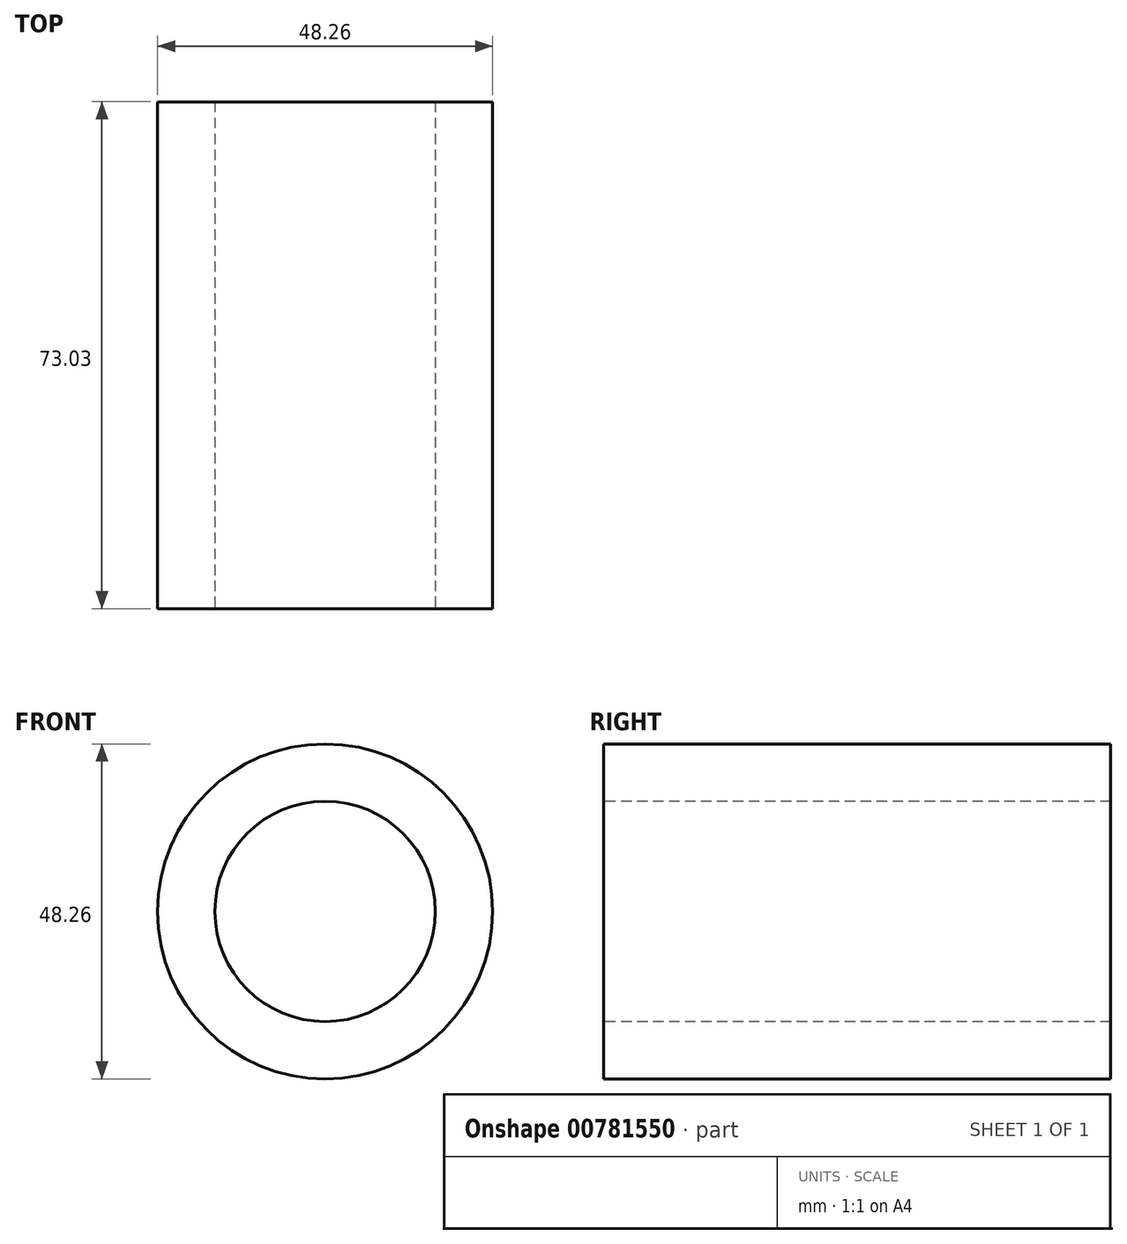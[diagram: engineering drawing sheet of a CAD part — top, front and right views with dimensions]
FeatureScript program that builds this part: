
annotation { "Feature Type Name" : "Feature", "Feature Type Description" : "" }
export const myFeature = defineFeature(function(context is Context, id is Id, definition is map)
    precondition{}
    {
        {
            var Q0;
            Q0=qCreatedBy(makeId("Front.planeOp"),FACE);
            var sketch = newSketch(context, id + "F0", { "sketchPlane" : qUnion([Q0])});
            skCircle(sketch, "E0", {"center": v(0, 0) * mm, "radius": 15.88 * mm});
            skCircle(sketch, "E1", {"center": v(0, 0) * mm, "radius": 24.13 * mm});
            skSolve(sketch);
        }
        {
            var Q0;
            Q0=makeQuery(id+"F0.imprint","IMPRINT",FACE,{"disambiguationData":[TD([[makeQuery(id+"F0.imprint","IMPRINT",EDGE,{"derivedFrom":sQuery(id+"F0.wireOp",EDGE,"E0")}),-1.0]])]});
            extrude(context, id + "F1", {"entities" : qUnion([Q0]), "oppositeDirection" : true, "depth" : 73.02 * mm, "offsetDistance" : 25.4 * mm});
        }
    });
